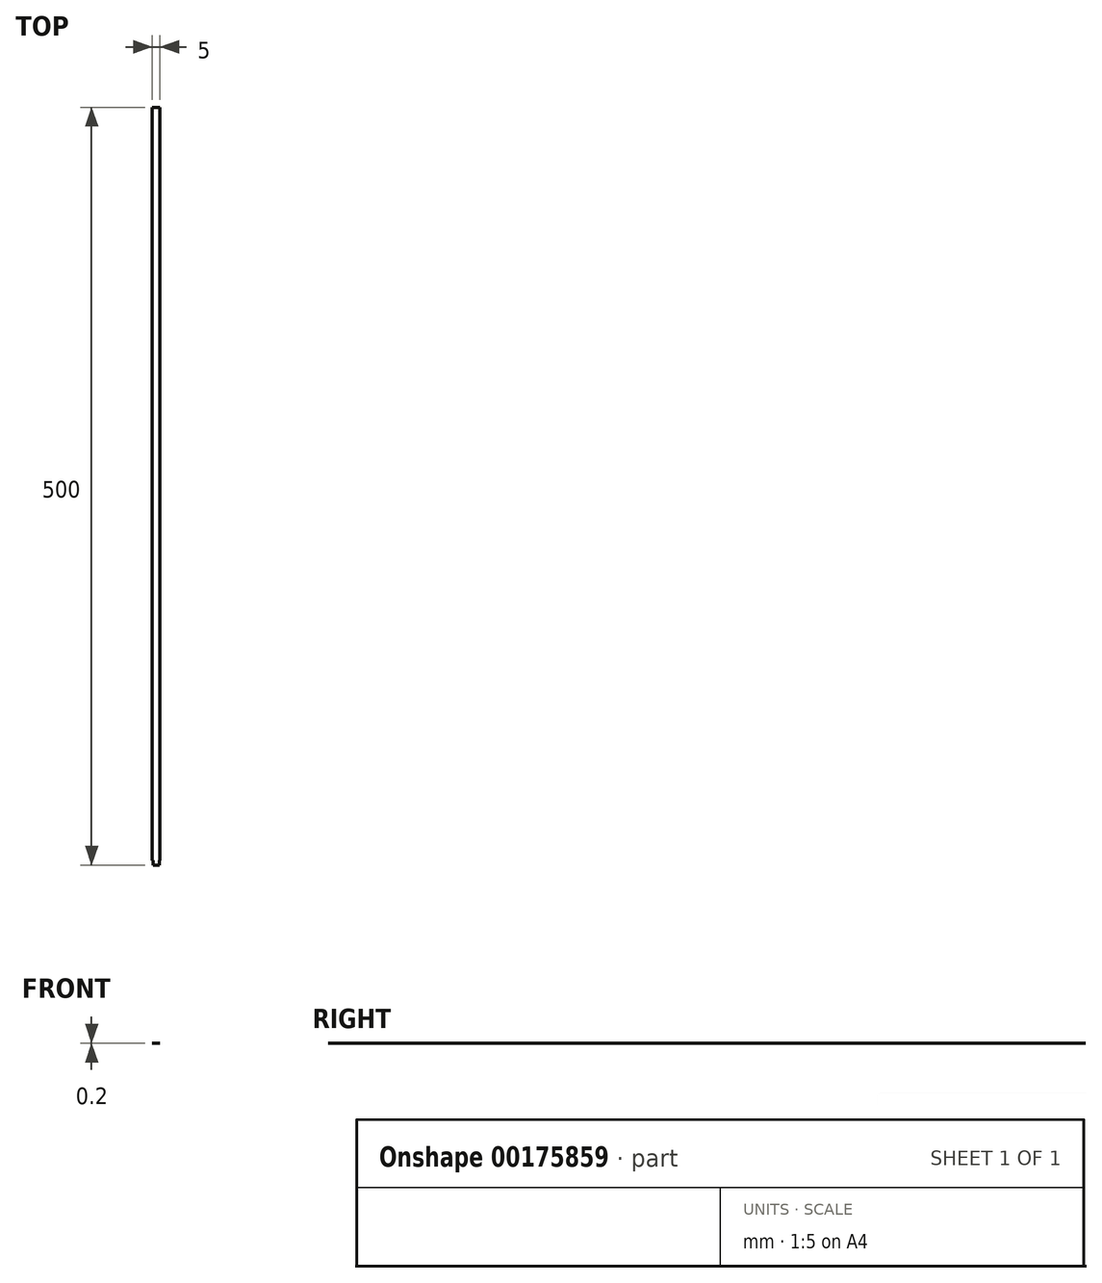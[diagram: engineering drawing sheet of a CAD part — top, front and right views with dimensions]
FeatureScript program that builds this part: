
annotation { "Feature Type Name" : "Feature", "Feature Type Description" : "" }
export const myFeature = defineFeature(function(context is Context, id is Id, definition is map)
    precondition{}
    {
        {
            var Q0;
            Q0=qCreatedBy(makeId("Top.planeOp"),FACE);
            var sketch = newSketch(context, id + "F0", { "sketchPlane" : qUnion([Q0])});
            skLineSegment(sketch, "E0.bottom", {"start": v(-4.5, 504.27) * mm, "end": v(0.5, 504.27) * mm});
            skLineSegment(sketch, "E0.top", {"start": v(-4.5, 4.27) * mm, "end": v(0.5, 4.27) * mm});
            skLineSegment(sketch, "E0.left", {"start": v(-4.5, 504.27) * mm, "end": v(-4.5, 4.27) * mm});
            skLineSegment(sketch, "E0.right", {"start": v(0.5, 504.27) * mm, "end": v(0.5, 4.27) * mm});
            skLineSegment(sketch, "E1.bottom", {"start": v(-4.5, 4.27) * mm, "end": v(-4, 4.27) * mm});
            skLineSegment(sketch, "E1.top", {"start": v(-4.5, 7.27) * mm, "end": v(-4, 7.27) * mm});
            skLineSegment(sketch, "E1.left", {"start": v(-4.5, 4.27) * mm, "end": v(-4.5, 7.27) * mm});
            skLineSegment(sketch, "E1.right", {"start": v(-4, 4.27) * mm, "end": v(-4, 7.27) * mm});
            skLineSegment(sketch, "E2.bottom", {"start": v(0.5, 4.27) * mm, "end": v(0, 4.27) * mm});
            skLineSegment(sketch, "E2.top", {"start": v(0.5, 7.27) * mm, "end": v(0, 7.27) * mm});
            skLineSegment(sketch, "E2.left", {"start": v(0.5, 4.27) * mm, "end": v(0.5, 7.27) * mm});
            skLineSegment(sketch, "E2.right", {"start": v(0, 4.27) * mm, "end": v(0, 7.27) * mm});
            skSolve(sketch);
        }
        {
            var Q0;
            Q0=makeQuery(id+"F0.imprint","IMPRINT",FACE,{"disambiguationData":[TD([[makeQuery(id+"F0.imprint","IMPRINT",EDGE,{"derivedFrom":sQuery(id+"F0.wireOp",EDGE,"E0.bottom")}),-1.0]])]});
            extrude(context, id + "F1", {"entities" : qUnion([Q0]), "depth" : .2 * mm});
        }
    });
